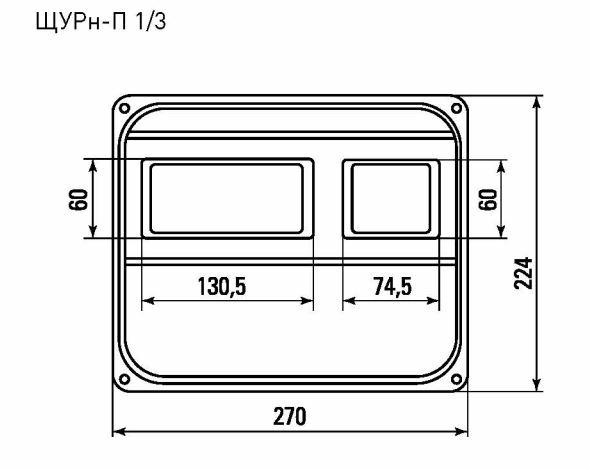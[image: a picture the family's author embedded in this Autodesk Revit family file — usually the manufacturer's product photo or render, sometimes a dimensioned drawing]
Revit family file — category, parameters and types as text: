
# Revit family: EKF_EE_Короб_КЭТ_Транзитный(1200х300х150)_Basic
name_source: partatom
category: Электрооборудование
units: mm (PartAtom-declared; Revit-internal decimal feet)

## family parameters
Всегда вертикально = Да
На основе рабочей плоскости = Нет
Общий = Нет
При загрузке вырезать с полостями = Нет
Размер круглого соединителя = Использовать диаметр
Тип детали = Силовой щит
Точка расчета площади = Да

## types (1)
- Короб КЭТ транзитный (1200х300х150) EKF Basic
    ADSK_Единица измерения = компл.
    ADSK_Завод-изготовитель = EKF
    ADSK_Классификация нагрузок = Прочее
    ADSK_Код изделия = uerm2-ket-t-1200-bas
    ADSK_Количество = 1
    ADSK_Количество фаз = 3
    ADSK_Коэффициент мощности = 1
    ADSK_Марка = Короб КЭТ транзитный
    ADSK_Масса = 0
    ADSK_Материал = RAL 7035_Сталь
    ADSK_Наименование = Короб КЭТ транзитный (1200х300х150) EKF BasicКороб КЭТ транзитный (1200х300х150) EKF Basic
    ADSK_Напряжение = 400 В
    ADSK_Номинальная мощность = 0 Вт
    ADSK_Обозначение = Короб КЭТ транзитный
    ADSK_Полная мощность = 0 В·А
    ADSK_Размер_Высота = 1200 мм
    ADSK_Размер_Глубина = 150 мм
    ADSK_Размер_Ширина = 300 мм
    ADSK_Ток = 125 А
    Изготовитель = EKF
    Количество DIN-реек = 0
    Количество модулей на DIN-рейке = 0
    Максимальное количество модулей = 0
    Описание = Короб КЭТ транзитный (1200х300х150) EKF BasicКороб КЭТ транзитный (1200х300х150) EKF Basic
    Серия номенклатуры = Basic
    Степень защиты IP = IP31
    ТВ = EKF
    Тип = 212 мм
    Тип установки = Навесной
